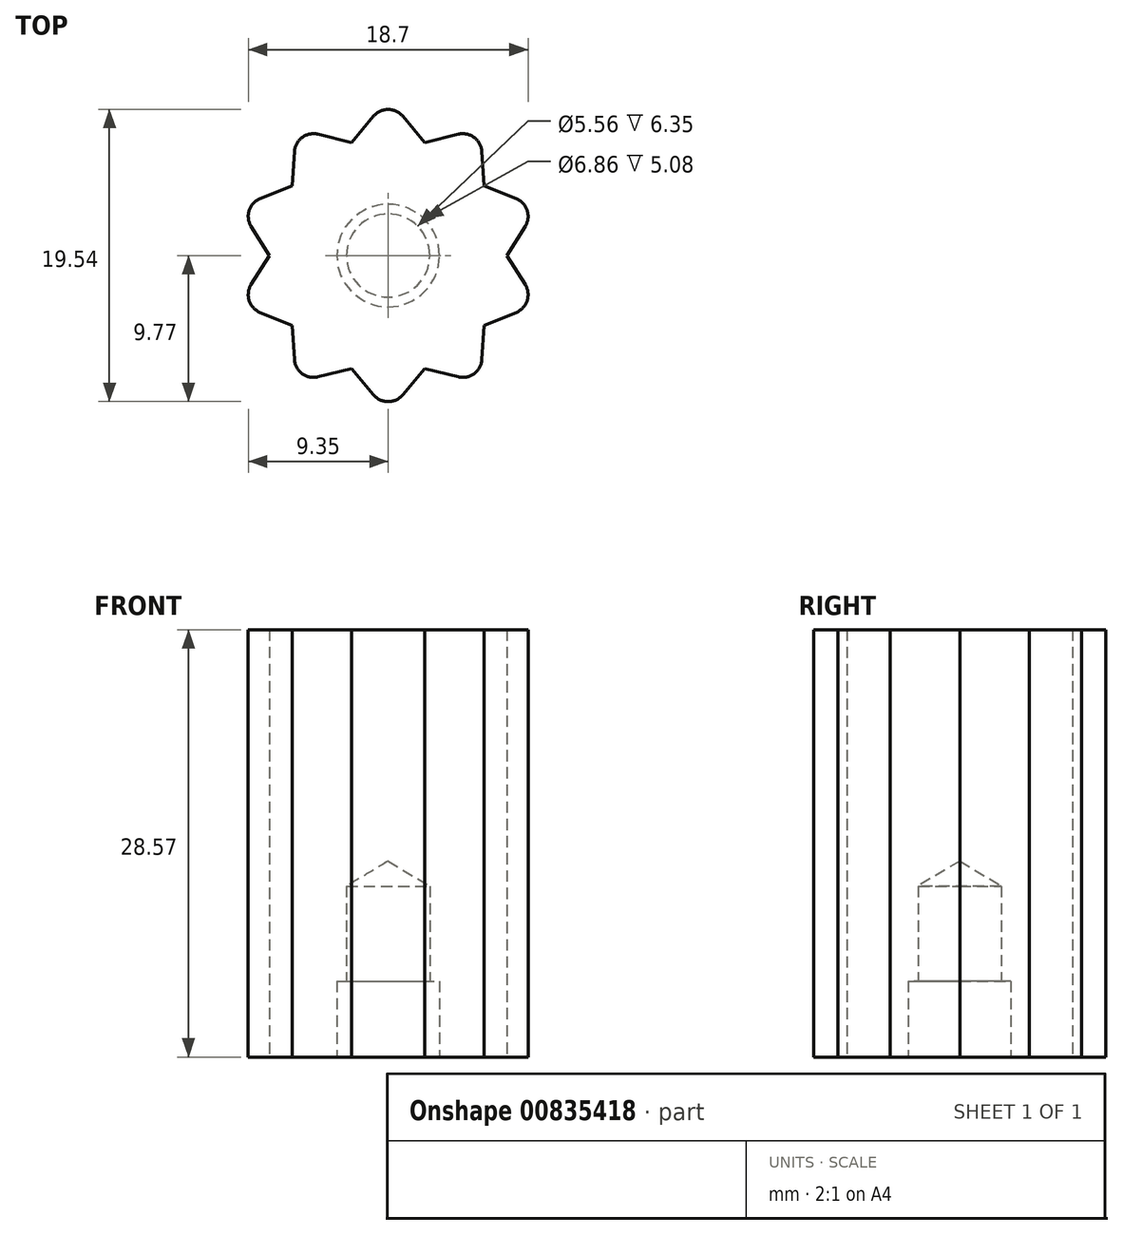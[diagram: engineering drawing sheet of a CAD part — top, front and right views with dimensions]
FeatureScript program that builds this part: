
annotation { "Feature Type Name" : "Feature", "Feature Type Description" : "" }
export const myFeature = defineFeature(function(context is Context, id is Id, definition is map)
    precondition{}
    {
        {
            var Q0;
            Q0=qCreatedBy(makeId("Top.planeOp"),FACE);
            var sketch = newSketch(context, id + "F0", { "sketchPlane" : qUnion([Q0])});
            skCircle(sketch, "E0", {"center": v(0, 0) * mm, "radius": 2.78 * mm, "construction": true});
            skCircle(sketch, "E1", {"center": v(0, 0) * mm, "radius": 7.94 * mm, "construction": true});
            skPoint(sketch, "E2", {"position": v(0, 10.48) * mm});
            skPoint(sketch, "E3", {"position": v(0, 7.94) * mm});
            skPoint(sketch, "E4.1.0", {"position": v(-6.16, 8.48) * mm});
            skPoint(sketch, "E4.2.0", {"position": v(-9.96, 3.24) * mm});
            skPoint(sketch, "E4.3.0", {"position": v(-9.96, -3.24) * mm});
            skPoint(sketch, "E4.4.0", {"position": v(-6.16, -8.48) * mm});
            skPoint(sketch, "E4.5.0", {"position": v(0, -10.48) * mm});
            skPoint(sketch, "E4.6.0", {"position": v(6.16, -8.48) * mm});
            skPoint(sketch, "E4.7.0", {"position": v(9.96, -3.24) * mm});
            skPoint(sketch, "E4.8.0", {"position": v(9.96, 3.24) * mm});
            skPoint(sketch, "E4.9.0", {"position": v(6.16, 8.48) * mm});
            skPoint(sketch, "E5.1.0", {"position": v(-2.45, 7.55) * mm});
            skPoint(sketch, "E5.2.0", {"position": v(-4.67, 6.42) * mm});
            skPoint(sketch, "E5.3.0", {"position": v(-6.42, 4.67) * mm});
            skPoint(sketch, "E5.4.0", {"position": v(-7.55, 2.45) * mm});
            skPoint(sketch, "E5.5.0", {"position": v(-7.94, 0) * mm});
            skPoint(sketch, "E5.6.0", {"position": v(-7.55, -2.45) * mm});
            skPoint(sketch, "E5.7.0", {"position": v(-6.42, -4.67) * mm});
            skPoint(sketch, "E5.8.0", {"position": v(-4.67, -6.42) * mm});
            skPoint(sketch, "E5.9.0", {"position": v(-2.45, -7.55) * mm});
            skPoint(sketch, "E5.10.0", {"position": v(0, -7.94) * mm});
            skPoint(sketch, "E5.11.0", {"position": v(2.45, -7.55) * mm});
            skPoint(sketch, "E5.12.0", {"position": v(4.67, -6.42) * mm});
            skPoint(sketch, "E5.13.0", {"position": v(6.42, -4.67) * mm});
            skPoint(sketch, "E5.14.0", {"position": v(7.55, -2.45) * mm});
            skPoint(sketch, "E5.15.0", {"position": v(7.94, 0) * mm});
            skPoint(sketch, "E5.16.0", {"position": v(7.55, 2.45) * mm});
            skPoint(sketch, "E5.17.0", {"position": v(6.42, 4.67) * mm});
            skPoint(sketch, "E5.18.0", {"position": v(4.67, 6.42) * mm});
            skPoint(sketch, "E5.19.0", {"position": v(2.45, 7.55) * mm});
            skLineSegment(sketch, "E6", {"start": v(0.97, 9.32) * mm, "end": v(2.45, 7.55) * mm});
            skLineSegment(sketch, "E7", {"start": v(2.45, 7.55) * mm, "end": v(4.69, 8.1) * mm});
            skLineSegment(sketch, "E8", {"start": v(6.26, 6.96) * mm, "end": v(6.42, 4.67) * mm});
            skLineSegment(sketch, "E9", {"start": v(6.42, 4.67) * mm, "end": v(8.56, 3.8) * mm});
            skLineSegment(sketch, "E10", {"start": v(9.16, 1.95) * mm, "end": v(7.94, 0) * mm});
            skLineSegment(sketch, "E11", {"start": v(7.94, 0) * mm, "end": v(9.16, -1.95) * mm});
            skLineSegment(sketch, "E12", {"start": v(8.56, -3.8) * mm, "end": v(6.42, -4.67) * mm});
            skLineSegment(sketch, "E13", {"start": v(6.42, -4.67) * mm, "end": v(6.26, -6.96) * mm});
            skLineSegment(sketch, "E14", {"start": v(4.69, -8.1) * mm, "end": v(2.45, -7.55) * mm});
            skLineSegment(sketch, "E15", {"start": v(2.45, -7.55) * mm, "end": v(0.97, -9.32) * mm});
            skLineSegment(sketch, "E16", {"start": v(-0.97, -9.32) * mm, "end": v(-2.45, -7.55) * mm});
            skLineSegment(sketch, "E17", {"start": v(-2.45, -7.55) * mm, "end": v(-4.69, -8.1) * mm});
            skLineSegment(sketch, "E18", {"start": v(-6.26, -6.96) * mm, "end": v(-6.42, -4.67) * mm});
            skLineSegment(sketch, "E19", {"start": v(-6.42, -4.67) * mm, "end": v(-8.56, -3.8) * mm});
            skLineSegment(sketch, "E20", {"start": v(-9.16, -1.95) * mm, "end": v(-7.94, 0) * mm});
            skLineSegment(sketch, "E21", {"start": v(-7.94, 0) * mm, "end": v(-9.16, 1.95) * mm});
            skLineSegment(sketch, "E22", {"start": v(-8.56, 3.8) * mm, "end": v(-6.42, 4.67) * mm});
            skLineSegment(sketch, "E23", {"start": v(-6.42, 4.67) * mm, "end": v(-6.26, 6.96) * mm});
            skLineSegment(sketch, "E24", {"start": v(-4.69, 8.1) * mm, "end": v(-2.45, 7.55) * mm});
            skLineSegment(sketch, "E25", {"start": v(-2.45, 7.55) * mm, "end": v(-0.97, 9.32) * mm});
            skArc(sketch, "E26.filletArc", {"start": v(0.97, 9.32) * mm, "mid": v(0, 9.77) * mm, "end": v(-0.97, 9.32) * mm});
            skArc(sketch, "E27.filletArc", {"start": v(6.26, 6.96) * mm, "mid": v(5.74, 7.9) * mm, "end": v(4.69, 8.1) * mm});
            skArc(sketch, "E28.filletArc", {"start": v(9.16, 1.95) * mm, "mid": v(9.3, 3.02) * mm, "end": v(8.56, 3.8) * mm});
            skArc(sketch, "E29.filletArc", {"start": v(8.56, -3.8) * mm, "mid": v(9.3, -3.02) * mm, "end": v(9.16, -1.95) * mm});
            skArc(sketch, "E30.filletArc", {"start": v(4.69, -8.1) * mm, "mid": v(5.74, -7.9) * mm, "end": v(6.26, -6.96) * mm});
            skArc(sketch, "E31.filletArc", {"start": v(-0.97, -9.32) * mm, "mid": v(0, -9.77) * mm, "end": v(0.97, -9.32) * mm});
            skArc(sketch, "E32.filletArc", {"start": v(-6.26, -6.96) * mm, "mid": v(-5.74, -7.9) * mm, "end": v(-4.69, -8.1) * mm});
            skArc(sketch, "E33.filletArc", {"start": v(-9.16, -1.95) * mm, "mid": v(-9.3, -3.02) * mm, "end": v(-8.56, -3.8) * mm});
            skArc(sketch, "E34.filletArc", {"start": v(-8.56, 3.8) * mm, "mid": v(-9.3, 3.02) * mm, "end": v(-9.16, 1.95) * mm});
            skArc(sketch, "E35.filletArc", {"start": v(-4.69, 8.1) * mm, "mid": v(-5.74, 7.9) * mm, "end": v(-6.26, 6.96) * mm});
            skSolve(sketch);
        }
        {
            var Q0;
            Q0 = qSketchRegion(id + "F0", true);
            extrude(context, id + "F1", {"entities" : qUnion([Q0]), "depth" : 28.57 * mm, "offsetDistance" : 25.4 * mm});
        }
        {
            var Q0;
            Q0=makeQuery(id+"F1.opExtrude","CAP_FACE",FACE,{"disambiguationData":[OSD([sQuery(id+"F0.wireOp",EDGE,"E6"),sQuery(id+"F0.wireOp",EDGE,"E7"),sQuery(id+"F0.wireOp",EDGE,"E8"),sQuery(id+"F0.wireOp",EDGE,"E9"),sQuery(id+"F0.wireOp",EDGE,"E10"),sQuery(id+"F0.wireOp",EDGE,"E11"),sQuery(id+"F0.wireOp",EDGE,"E12"),sQuery(id+"F0.wireOp",EDGE,"E13"),sQuery(id+"F0.wireOp",EDGE,"E14"),sQuery(id+"F0.wireOp",EDGE,"E15"),sQuery(id+"F0.wireOp",EDGE,"E16"),sQuery(id+"F0.wireOp",EDGE,"E17"),sQuery(id+"F0.wireOp",EDGE,"E18"),sQuery(id+"F0.wireOp",EDGE,"E19"),sQuery(id+"F0.wireOp",EDGE,"E20"),sQuery(id+"F0.wireOp",EDGE,"E21"),sQuery(id+"F0.wireOp",EDGE,"E22"),sQuery(id+"F0.wireOp",EDGE,"E23"),sQuery(id+"F0.wireOp",EDGE,"E24"),sQuery(id+"F0.wireOp",EDGE,"E25"),sQuery(id+"F0.wireOp",EDGE,"E26.filletArc"),sQuery(id+"F0.wireOp",EDGE,"E27.filletArc"),sQuery(id+"F0.wireOp",EDGE,"E28.filletArc"),sQuery(id+"F0.wireOp",EDGE,"E29.filletArc"),sQuery(id+"F0.wireOp",EDGE,"E30.filletArc"),sQuery(id+"F0.wireOp",EDGE,"E31.filletArc"),sQuery(id+"F0.wireOp",EDGE,"E32.filletArc"),sQuery(id+"F0.wireOp",EDGE,"E33.filletArc"),sQuery(id+"F0.wireOp",EDGE,"E34.filletArc"),sQuery(id+"F0.wireOp",EDGE,"E35.filletArc")])],"isStart":true});
            var sketch = newSketch(context, id + "F2", { "sketchPlane" : qUnion([Q0])});
            skPoint(sketch, "E36", {"position": v(0, 0) * mm});
            skSolve(sketch);
        }
        {
            var Q0;
            Q0=sQuery(id+"F2.wireOp",VERTEX,"E36");
            var Q1;
            Q1=makeQuery(id+"F1.opExtrude","SWEPT_BODY",BODY,{"disambiguationData":[OSD([sQuery(id+"F0.wireOp",EDGE,"E6"),sQuery(id+"F0.wireOp",EDGE,"E7"),sQuery(id+"F0.wireOp",EDGE,"E8"),sQuery(id+"F0.wireOp",EDGE,"E9"),sQuery(id+"F0.wireOp",EDGE,"E10"),sQuery(id+"F0.wireOp",EDGE,"E11"),sQuery(id+"F0.wireOp",EDGE,"E12"),sQuery(id+"F0.wireOp",EDGE,"E13"),sQuery(id+"F0.wireOp",EDGE,"E14"),sQuery(id+"F0.wireOp",EDGE,"E15"),sQuery(id+"F0.wireOp",EDGE,"E16"),sQuery(id+"F0.wireOp",EDGE,"E17"),sQuery(id+"F0.wireOp",EDGE,"E18"),sQuery(id+"F0.wireOp",EDGE,"E19"),sQuery(id+"F0.wireOp",EDGE,"E20"),sQuery(id+"F0.wireOp",EDGE,"E21"),sQuery(id+"F0.wireOp",EDGE,"E22"),sQuery(id+"F0.wireOp",EDGE,"E23"),sQuery(id+"F0.wireOp",EDGE,"E24"),sQuery(id+"F0.wireOp",EDGE,"E25"),sQuery(id+"F0.wireOp",EDGE,"E26.filletArc"),sQuery(id+"F0.wireOp",EDGE,"E27.filletArc"),sQuery(id+"F0.wireOp",EDGE,"E28.filletArc"),sQuery(id+"F0.wireOp",EDGE,"E29.filletArc"),sQuery(id+"F0.wireOp",EDGE,"E30.filletArc"),sQuery(id+"F0.wireOp",EDGE,"E31.filletArc"),sQuery(id+"F0.wireOp",EDGE,"E32.filletArc"),sQuery(id+"F0.wireOp",EDGE,"E33.filletArc"),sQuery(id+"F0.wireOp",EDGE,"E34.filletArc"),sQuery(id+"F0.wireOp",EDGE,"E35.filletArc")])]});
            hole(context, id + "F3", {"style" : HoleStyle.C_BORE, "endStyle" : HoleEndStyle.BLIND, "holeDiameter" : 5.56 * mm, "cBoreDiameter" : 6.86 * mm, "cBoreDepth" : 5.08 * mm, "majorDiameter" : 6.35 * mm, "holeDepth" : 11.43 * mm, "isTappedThrough" : true, "tappedDepth" : 12.7 * mm, "tapClearance" : 3, "startFromSketch" : true, "locations" : qUnion([Q0]), "scope" : qUnion([Q1])});
        }
    });
